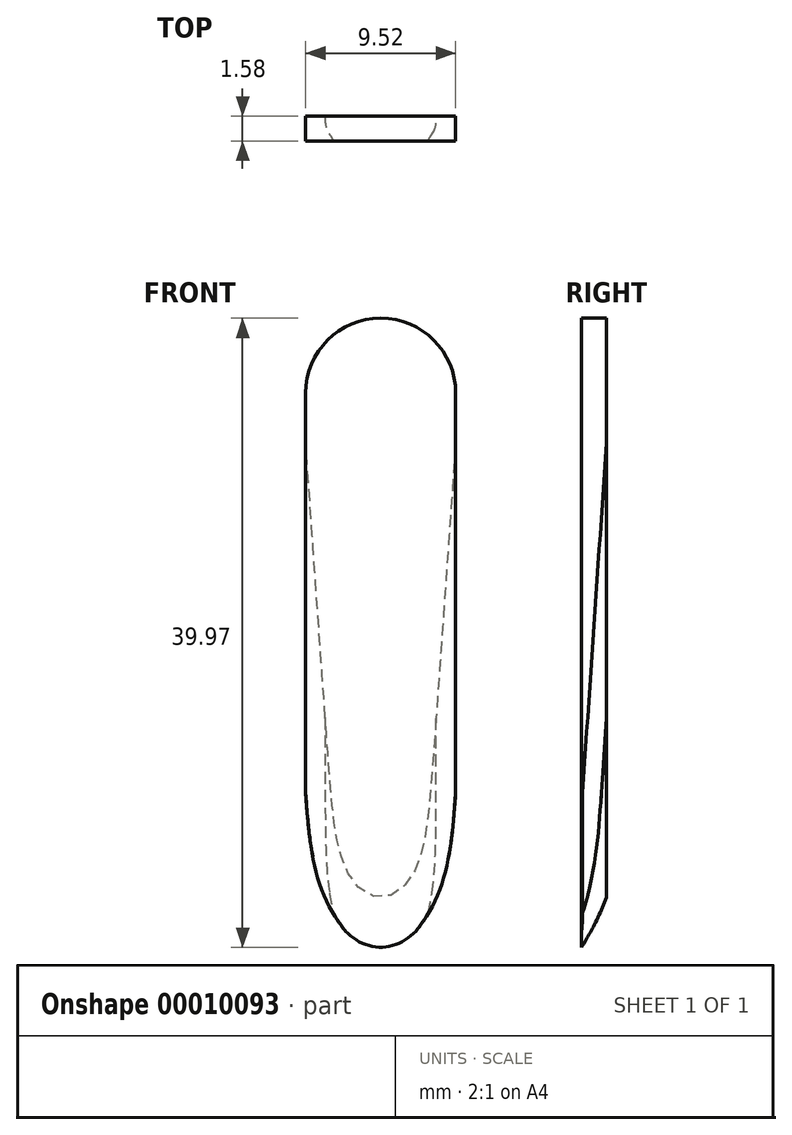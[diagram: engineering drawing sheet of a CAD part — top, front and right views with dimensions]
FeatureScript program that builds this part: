
annotation { "Feature Type Name" : "Feature", "Feature Type Description" : "" }
export const myFeature = defineFeature(function(context is Context, id is Id, definition is map)
    precondition{}
    {
        {
            var Q0;
            Q0=qCreatedBy(makeId("Front.planeOp"),FACE);
            var sketch = newSketch(context, id + "F0", { "sketchPlane" : qUnion([Q0])});
            skLineSegment(sketch, "E0.rect.left", {"start": v(4.76, 6.35) * mm, "end": v(4.76, -19.05) * mm});
            skLineSegment(sketch, "E0.rect.right", {"start": v(-4.76, 6.35) * mm, "end": v(-4.76, -19.05) * mm});
            skPoint(sketch, "E0.rect.middle", {"position": v(0, 0) * mm});
            skFitSpline(sketch, "E1", {"points": [v(4.76, -19.05) * mm, v(3.53, -25.72) * mm, v(0, -30.16) * mm], "startDerivative": vector(-0.97, -13.66) * mm, "endDerivative": vector(-8.7, -7.83) * mm});
            skFitSpline(sketch, "E2.MirrorCS", {"points": [v(-4.76, -19.05) * mm, v(-3.53, -25.72) * mm, v(0, -30.16) * mm], "startDerivative": vector(0.97, -13.66) * mm, "endDerivative": vector(8.7, -7.83) * mm});
            skArc(sketch, "E3", {"start": v(4.76, 6.35) * mm, "mid": v(0, 11.11) * mm, "end": v(-4.76, 6.35) * mm});
            skPoint(sketch, "E4.center.orphan", {"position": v(0, 19.05) * mm});
            skPoint(sketch, "E5.orphan", {"position": v(4.76, 19.05) * mm});
            skPoint(sketch, "E6.orphan", {"position": v(-4.76, 19.05) * mm});
            skSolve(sketch);
        }
        {
            var Q0;
            Q0 = qSketchRegion(id + "F0", true);
            extrude(context, id + "F1", {"entities" : qUnion([Q0]), "endBound" : BoundingType.SYMMETRIC, "depth" : 1.59 * mm});
        }
        {
            var Q0;
            Q0=makeQuery(id+"F1.opExtrude","CAP_EDGE",EDGE,{"disambiguationData":[OSD([sQuery(id+"F0.wireOp",EDGE,"E1")])],"isStart":true});
            var Q1;
            Q1=makeQuery(id+"F1.opExtrude","CAP_EDGE",EDGE,{"disambiguationData":[OSD([sQuery(id+"F0.wireOp",EDGE,"E2.MirrorCS")])],"isStart":true});
            chamfer(context, id + "F2", {"entities" : qUnion([Q0, Q1]), "chamferType" : ChamferType.TWO_OFFSETS, "width1" : 1.57 * mm, "oppositeDirection" : false, "width2" : 1.52 * mm});
        }
        {
            var Q0;
            Q0=makeQuery(id+"F2.opChamfer","BLEND_EDGE",EDGE,{"blendedFrom":[makeQuery(id+"F1.opExtrude","CAP_EDGE",EDGE,{"disambiguationData":[OSD([sQuery(id+"F0.wireOp",EDGE,"E1")])],"isStart":true}),makeQuery(id+"F1.opExtrude","CAP_EDGE",EDGE,{"disambiguationData":[OSD([sQuery(id+"F0.wireOp",EDGE,"E2.MirrorCS")])],"isStart":true})],"blendedInto":[]});
            fillet(context, id + "F3", {"entities" : qUnion([Q0]), "radius" : 5.08 * mm, "tangentPropagation" : true, "allowEdgeOverflow" : false});
        }
    });
